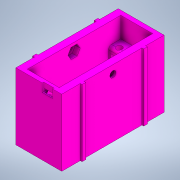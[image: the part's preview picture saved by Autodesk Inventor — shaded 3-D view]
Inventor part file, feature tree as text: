
AUTODESK INVENTOR PART (.ipt)
format: ipt  version: 2020 (Build 240168000, 168)  size: 383,488 bytes
history: native  units: mm
features: extrude x14, sketch x12, fillet x3, projected_geometry x2, plane x1, draft x1
ambient origin geometry x8: Origin, YZ Plane, XZ Plane, XY Plane, X Axis, Y Axis, Z Axis, Center Point
bodies: Solid1 (feature_tree)
feature tree (33):
  sketch  "Sketch1"  dims[d0=31.0mm d1=67.0mm]
  extrude  "Extrusion1"  Depth=67.0mm
  extrude  "Extrusion2"  Depth=44.6mm
  extrude  "Extrusion3"  Depth=58.0mm TaperAngle=0.0deg
  extrude  "Extrusion4"  Depth=20.0mm TaperAngle=0.0deg
  extrude  "Extrusion6"  Depth=3.6mm
  extrude  "Extrusion7"  TaperAngle=0.0deg  [1 undecoded]
  sketch  "Sketch8"  dims[d13=28.2mm d15=0.0mm d16=0.0mm]
  extrude  "Extrusion8"  Depth=8.0mm
  extrude  "Extrusion9"  Depth=4.0mm TaperAngle=0.0deg
  fillet  "Fillet1"  Radius=5.0mm
  fillet  "Fillet2"  Radius=3.0mm
  fillet  "Fillet4"  Radius=10.0mm
  extrude  "Extrusion11"  Depth=3.0mm TaperAngle=0.0deg
  extrude  "Extrusion12"  Depth=9.0mm
  plane  "Work Plane1"
  extrude  "Extrusion13"  Depth=3.0mm
  extrude  "Extrusion14"  Depth=1.5mm
  extrude  "Extrusion15"  Depth=1.5mm TaperAngle=0.0deg
  draft  "FaceDraft1"
  extrude  "Extrusion16"  Depth=1.5mm
  sketch  "Sketch2"  dims[d2=44.6mm d3=99.6mm]
  projected_geometry  "Projected Loop1"
  sketch  "Sketch3"  dims[d4=7.0mm d5=0.0mm d6=58.0mm d7=0.0mm]
  sketch  "Sketch6"  dims[d8=12.0mm d9=20.0mm d10=0.0mm]
  sketch  "Sketch7"  dims[d11=1.8mm d12=3.6mm]
  sketch  "Sketch10"  dims[d18=6.0mm d19=8.0mm]
  sketch  "Sketch11"  dims[d23=7.0mm d24=4.0mm d25=0.0mm d26=5.0mm d27=0.0mm d28=3.0mm d29=10.0mm]
  sketch  "Sketch12"  dims[d30=5.0mm d31=3.0mm d32=0.0mm]
  projected_geometry  "Projected Loop2"
  sketch  "Sketch13"  dims[d33=96.0mm d34=0.0mm d36=9.0mm]
  sketch  "Sketch14"  dims[d37=7.0mm d38=3.0mm]
  sketch  "Sketch15"  dims[d44=3.0mm d45=10.4mm d46=35.8mm d47=4.8mm d48=0.0mm d49=0.0mm d50=5.5mm d51=17.6mm d52=75.0mm d53=50.0mm d54=0.0mm d55=-10.0mm d56=8.5mm d57=4.5mm d58=0.0mm d59=2.0mm d60=0.0mm d61=7.0mm d62=0.0mm d63=-0.523599mm d64=1.5mm d65=0.0mm]
note: 1 required parameter value undecoded (feature->parameter linkage not recoverable at this tier; creation-order binding heuristic only, values carry confidence <= 0.55)
